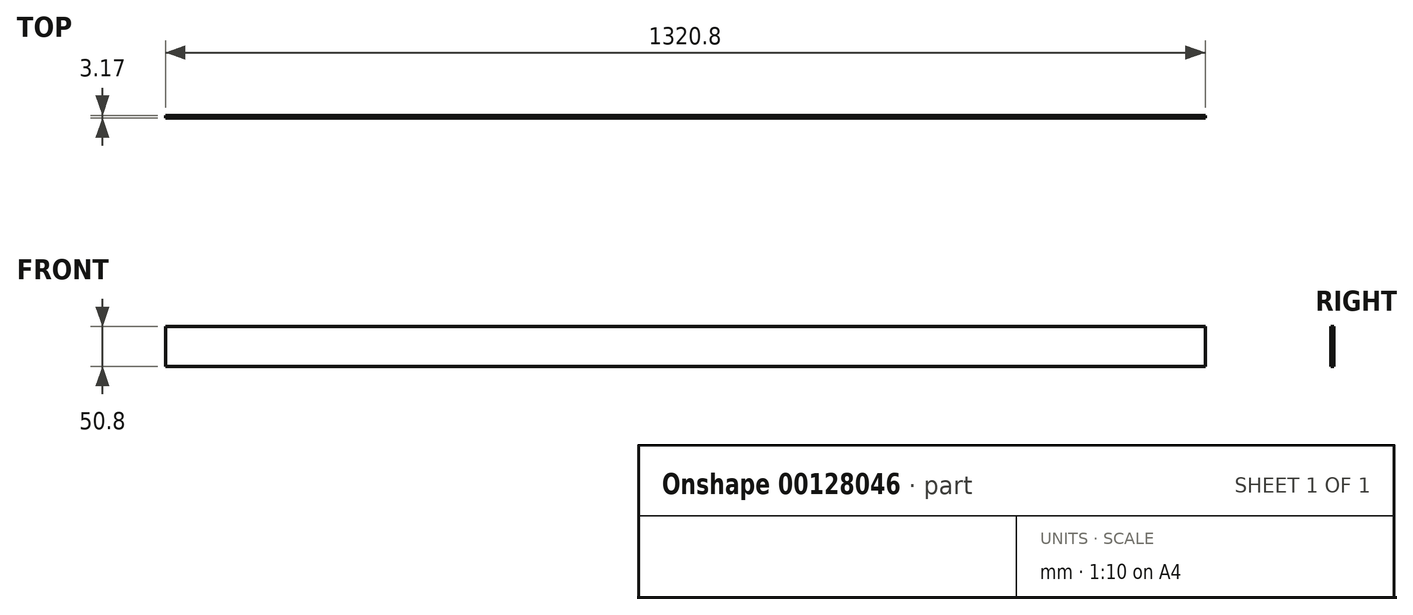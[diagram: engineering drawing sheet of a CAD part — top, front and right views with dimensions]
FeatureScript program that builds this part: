
annotation { "Feature Type Name" : "Feature", "Feature Type Description" : "" }
export const myFeature = defineFeature(function(context is Context, id is Id, definition is map)
    precondition{}
    {
        {
            var Q0;
            Q0=qCreatedBy(makeId("Front.planeOp"),FACE);
            var sketch = newSketch(context, id + "F0", { "sketchPlane" : qUnion([Q0])});
            skLineSegment(sketch, "E0.bottom", {"start": v(661.8, 25.4) * mm, "end": v(-659, 25.4) * mm});
            skLineSegment(sketch, "E0.top", {"start": v(661.8, -25.4) * mm, "end": v(-659, -25.4) * mm});
            skLineSegment(sketch, "E0.left", {"start": v(661.8, 25.4) * mm, "end": v(661.8, -25.4) * mm});
            skLineSegment(sketch, "E0.right", {"start": v(-659, 25.4) * mm, "end": v(-659, -25.4) * mm});
            skPoint(sketch, "E0.middle", {"position": v(1.4, 0) * mm});
            skSolve(sketch);
        }
        {
            var Q0;
            Q0 = qSketchRegion(id + "F0", true);
            extrude(context, id + "F1", {"entities" : qUnion([Q0]), "depth" : 3.17 * mm});
        }
    });
